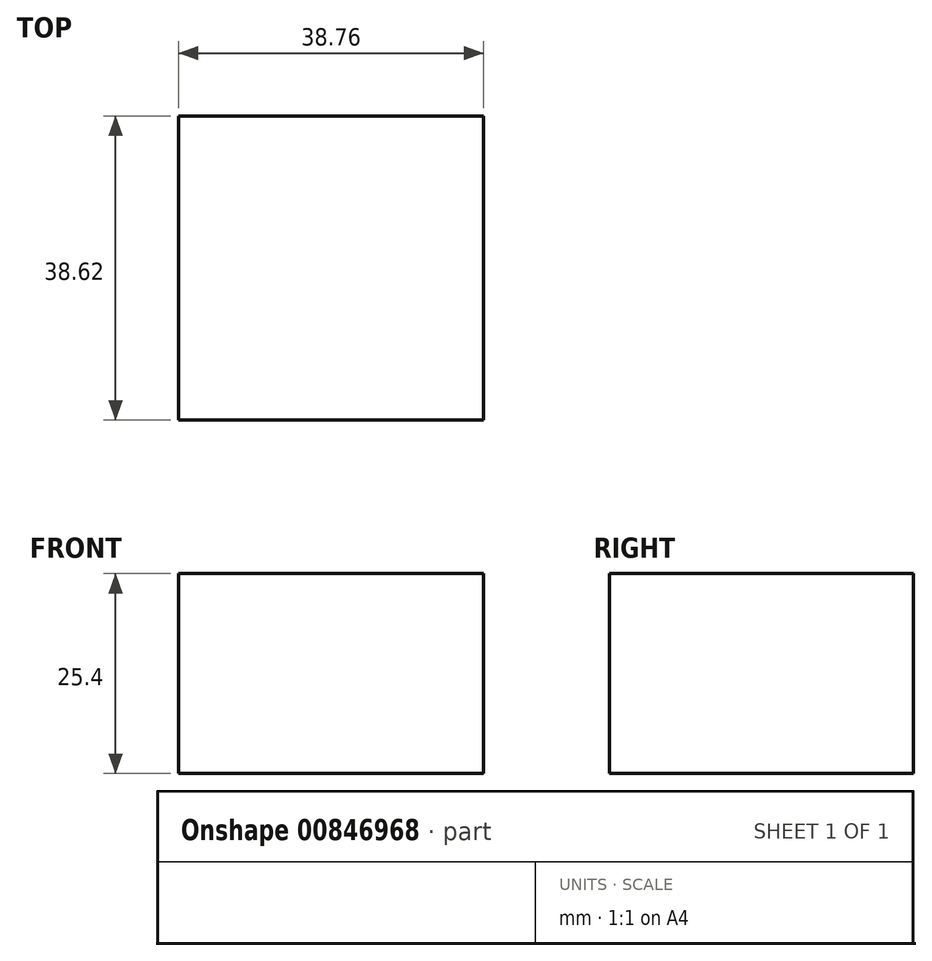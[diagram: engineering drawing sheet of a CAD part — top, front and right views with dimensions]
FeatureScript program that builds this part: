
annotation { "Feature Type Name" : "Feature", "Feature Type Description" : "" }
export const myFeature = defineFeature(function(context is Context, id is Id, definition is map)
    precondition{}
    {
        {
            var Q0;
            Q0=qCreatedBy(makeId("Top.planeOp"),FACE);
            var sketch = newSketch(context, id + "F0", { "sketchPlane" : qUnion([Q0])});
            skLineSegment(sketch, "E0.bottom", {"start": v(-38.76, 38.62) * mm, "end": v(0, 38.62) * mm});
            skLineSegment(sketch, "E0.top", {"start": v(-38.76, 0) * mm, "end": v(0, 0) * mm});
            skLineSegment(sketch, "E0.left", {"start": v(-38.76, 38.62) * mm, "end": v(-38.76, 0) * mm});
            skLineSegment(sketch, "E0.right", {"start": v(0, 38.62) * mm, "end": v(0, 0) * mm});
            skSolve(sketch);
        }
        {
            var Q0;
            Q0=sQuery(id+"F0.wireOp",EDGE,"E0.left");
            var Q1;
            Q1=sQuery(id+"F0.wireOp",EDGE,"E0.bottom");
            var Q2;
            Q2=sQuery(id+"F0.wireOp",EDGE,"E0.right");
            var Q3;
            Q3=sQuery(id+"F0.wireOp",EDGE,"E0.top");
            extrude(context, id + "F1", {"bodyType" : ToolBodyType.SURFACE, "surfaceEntities" : qUnion([Q0, Q1, Q2, Q3]), "depth" : 25.4 * mm, "offsetDistance" : 25.4 * mm});
        }
    });
